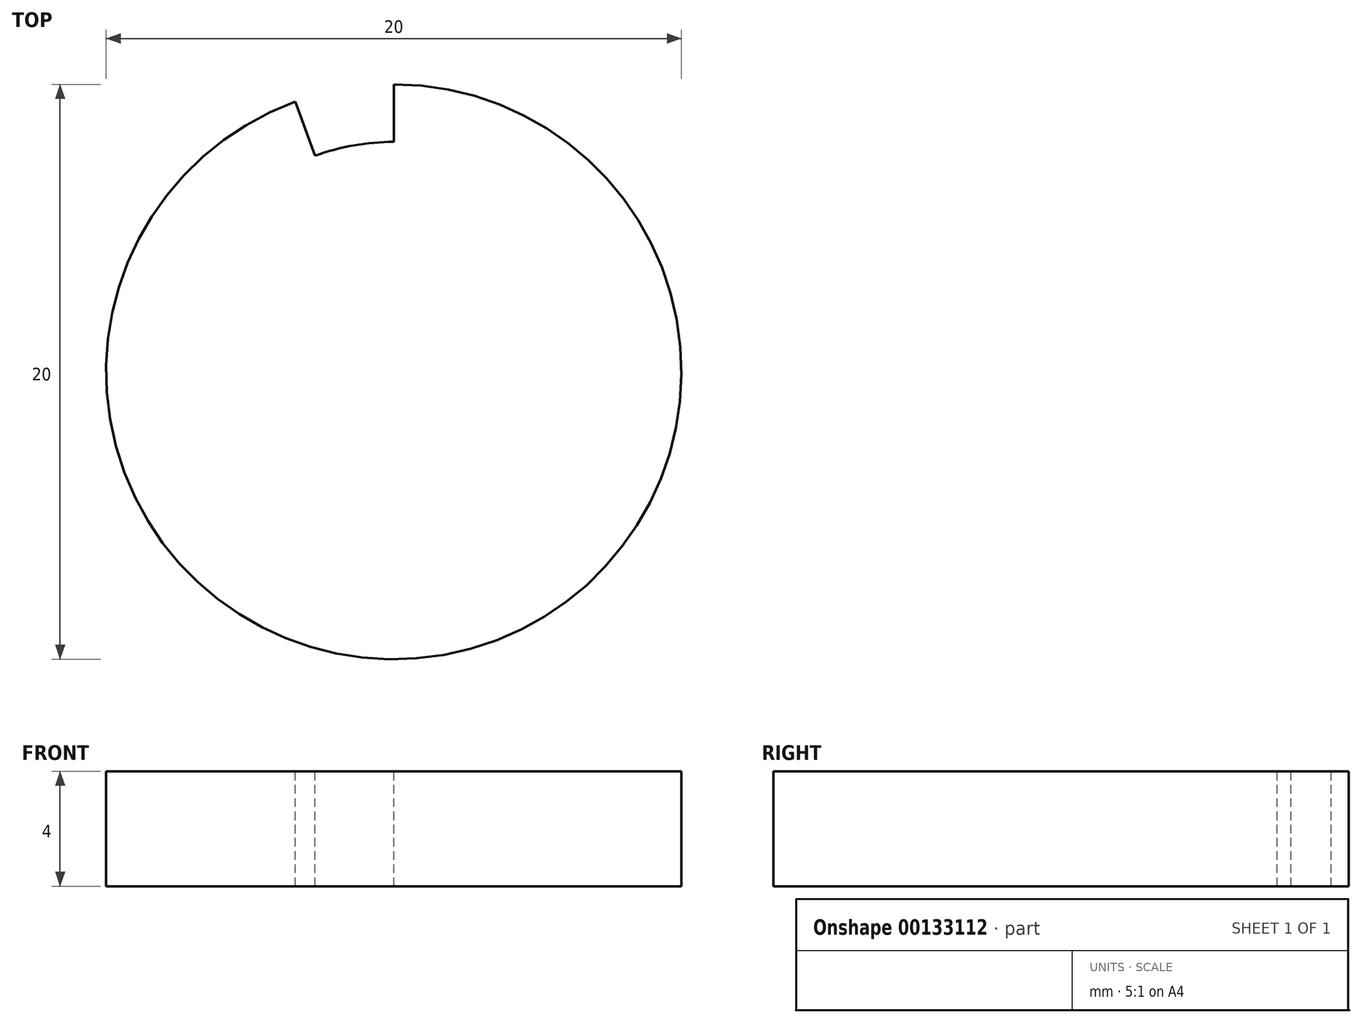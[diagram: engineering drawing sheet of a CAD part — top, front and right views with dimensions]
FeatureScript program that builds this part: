
annotation { "Feature Type Name" : "Feature", "Feature Type Description" : "" }
export const myFeature = defineFeature(function(context is Context, id is Id, definition is map)
    precondition{}
    {
        {
            var Q0;
            Q0=qCreatedBy(makeId("Top.planeOp"),FACE);
            var sketch = newSketch(context, id + "F0", { "sketchPlane" : qUnion([Q0])});
            skCircle(sketch, "E0", {"center": v(0, 0) * mm, "radius": 10 * mm});
            skSolve(sketch);
        }
        {
            var Q0;
            Q0 = qSketchRegion(id + "F0", true);
            extrude(context, id + "F1", {"entities" : qUnion([Q0]), "depth" : 4 * mm});
        }
        {
            var Q0;
            Q0=makeQuery(id+"F1.opExtrude","CAP_FACE",FACE,{"disambiguationData":[OSD([sQuery(id+"F0.wireOp",EDGE,"E0")])],"isStart":false});
            var sketch = newSketch(context, id + "F2", { "sketchPlane" : qUnion([Q0])});
            skCircle(sketch, "E1.0", {"center": v(0, 0) * mm, "radius": 8 * mm});
            skLineSegment(sketch, "E2", {"start": v(0, 0) * mm, "end": v(0, 12.25) * mm, "construction": true});
            skLineSegment(sketch, "E3", {"start": v(0, 0) * mm, "end": v(-4.9, 13.46) * mm, "construction": true});
            skPoint(sketch, "E4", {"position": v(-3.42, 9.4) * mm});
            skPoint(sketch, "E5", {"position": v(-2.74, 7.52) * mm});
            skPoint(sketch, "E6", {"position": v(0, 8) * mm});
            skPoint(sketch, "E7", {"position": v(0, 10) * mm});
            skLineSegment(sketch, "E8", {"start": v(-2.74, 7.52) * mm, "end": v(-3.42, 9.4) * mm});
            skLineSegment(sketch, "E9", {"start": v(0, 8) * mm, "end": v(0, 10) * mm});
            skSolve(sketch);
        }
        {
            var Q0;
            {var subQ0=sQuery(id+"F2.wireOp",EDGE,"E8");Q0=makeQuery(id+"F2.imprint","IMPRINT",FACE,{"disambiguationData":[TD([[makeQuery(id+"F2.imprint","IMPRINT",EDGE,{"derivedFrom":subQ0}),-1.0]])]});}
            extrude(context, id + "F3", {"entities" : qUnion([Q0]), "operationType" : NewBodyOperationType.REMOVE, "endBound" : BoundingType.THROUGH_ALL, "oppositeDirection" : true, "depth" : 25 * mm});
        }
        {
            var Q0;
            Q0=qCreatedBy(makeId("Front.planeOp"),FACE);
            var sketch = newSketch(context, id + "F4", { "sketchPlane" : qUnion([Q0])});
            skLineSegment(sketch, "E10", {"start": v(0, 0) * mm, "end": v(0, 82.1) * mm});
            skSolve(sketch);
        }
    });
